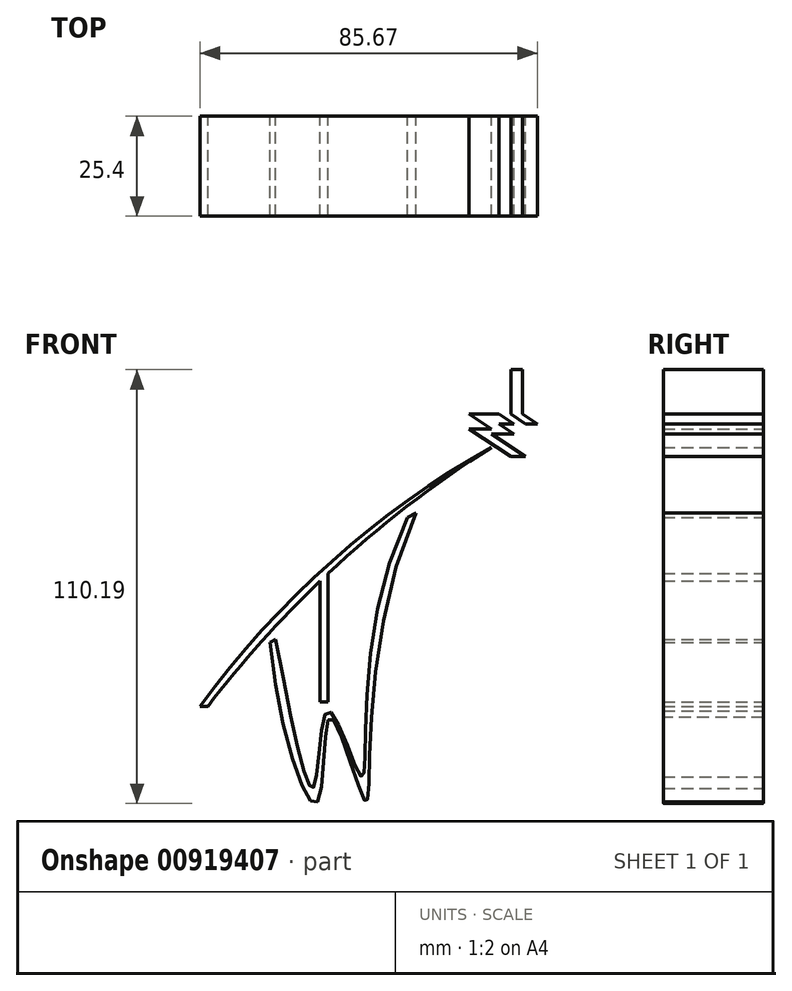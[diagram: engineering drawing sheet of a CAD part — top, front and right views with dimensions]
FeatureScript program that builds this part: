
annotation { "Feature Type Name" : "Feature", "Feature Type Description" : "" }
export const myFeature = defineFeature(function(context is Context, id is Id, definition is map)
    precondition{}
    {
        {
            var Q0;
            Q0=qCreatedBy(makeId("Front.planeOp"),FACE);
            var sketch = newSketch(context, id + "F0", { "sketchPlane" : qUnion([Q0])});
            skArc(sketch, "E0", {"start": v(27.94, 43.26) * mm, "mid": v(-11, 13.56) * mm, "end": v(-44.09, -22.54) * mm});
            skArc(sketch, "E1", {"start": v(27.94, 43.26) * mm, "mid": v(-12.59, 14.34) * mm, "end": v(-46.04, -22.54) * mm});
            skLineSegment(sketch, "E2", {"start": v(-46.04, -22.54) * mm, "end": v(-44.09, -22.54) * mm});
            skLineSegment(sketch, "E3", {"start": v(-15.57, 9.3) * mm, "end": v(-15.57, -21.37) * mm});
            skLineSegment(sketch, "E4", {"start": v(-15.57, -21.37) * mm, "end": v(-13.53, -21.37) * mm});
            skLineSegment(sketch, "E5", {"start": v(-13.53, -21.37) * mm, "end": v(-13.53, 11.23) * mm});
            skArc(sketch, "E6", {"start": v(27.94, 43.26) * mm, "mid": v(6.63, 28) * mm, "end": v(-13.53, 11.23) * mm});
            skArc(sketch, "E7", {"start": v(-15.57, 9.3) * mm, "mid": v(-30.23, -6.26) * mm, "end": v(-44.09, -22.54) * mm});
            skPoint(sketch, "E8.4.internal.snap0", {"position": v(-30.23, -6.26) * mm});
            skFitSpline(sketch, "E8", {"points": [v(8.74, 26.62) * mm, v(-4.43, -46.23) * mm, v(-12.97, -25.36) * mm, v(-16.13, -46.57) * mm, v(-28.33, -6.26) * mm], "startDerivative": vector(-136.03, -313.45) * mm, "endDerivative": vector(-22.87, 244.76) * mm});
            skPoint(sketch, "E9.0.internal.snap0", {"position": v(6.63, 28) * mm});
            skFitSpline(sketch, "E9", {"points": [v(6.63, 25.41) * mm, v(-5.36, -40.08) * mm, v(-13.53, -23.7) * mm, v(-17.03, -42.75) * mm, v(-26.85, -5.57) * mm], "startDerivative": vector(-126.44, -255.91) * mm, "endDerivative": vector(-44.36, 231) * mm});
            skLineSegment(sketch, "E10", {"start": v(-28.33, -6.26) * mm, "end": v(-26.85, -5.57) * mm});
            skLineSegment(sketch, "E11", {"start": v(6.63, 25.41) * mm, "end": v(8.74, 26.62) * mm});
            skArc(sketch, "E12", {"start": v(-19.48, 13.87) * mm, "mid": v(-23.54, 31.95) * mm, "end": v(-12.13, 17.35) * mm});
            skArc(sketch, "E13", {"start": v(-19.48, 11.53) * mm, "mid": v(-25.21, 33.72) * mm, "end": v(-9.43, 17.1) * mm});
            skLineSegment(sketch, "E14", {"start": v(-19.48, 13.87) * mm, "end": v(-19.48, 11.53) * mm});
            skLineSegment(sketch, "E15", {"start": v(-12.13, 17.35) * mm, "end": v(-9.43, 17.1) * mm});
            skLineSegment(sketch, "E16", {"start": v(32.91, 40.98) * mm, "end": v(22.26, 47.99) * mm});
            skLineSegment(sketch, "E17", {"start": v(22.26, 47.99) * mm, "end": v(27.94, 47.99) * mm});
            skLineSegment(sketch, "E18", {"start": v(27.94, 47.99) * mm, "end": v(22.26, 51.72) * mm});
            skLineSegment(sketch, "E19", {"start": v(22.26, 51.72) * mm, "end": v(29.9, 51.72) * mm});
            skLineSegment(sketch, "E20", {"start": v(29.9, 51.72) * mm, "end": v(33.7, 49.22) * mm});
            skLineSegment(sketch, "E21", {"start": v(33.7, 49.22) * mm, "end": v(29.9, 49.22) * mm});
            skLineSegment(sketch, "E22", {"start": v(29.9, 49.22) * mm, "end": v(33.7, 46.72) * mm});
            skLineSegment(sketch, "E23", {"start": v(33.7, 46.72) * mm, "end": v(27.94, 46.72) * mm});
            skLineSegment(sketch, "E24", {"start": v(27.94, 46.72) * mm, "end": v(36.66, 40.98) * mm});
            skLineSegment(sketch, "E25", {"start": v(36.66, 40.98) * mm, "end": v(32.91, 40.98) * mm});
            skLineSegment(sketch, "E26", {"start": v(32.91, 51.72) * mm, "end": v(36.66, 49.26) * mm});
            skLineSegment(sketch, "E27", {"start": v(36.66, 49.26) * mm, "end": v(39.63, 49.26) * mm});
            skLineSegment(sketch, "E28", {"start": v(39.63, 49.26) * mm, "end": v(35.88, 51.72) * mm});
            skLineSegment(sketch, "E29", {"start": v(35.88, 51.72) * mm, "end": v(35.88, 63.02) * mm});
            skLineSegment(sketch, "E30", {"start": v(32.91, 63.02) * mm, "end": v(35.88, 63.02) * mm});
            skLineSegment(sketch, "E31", {"start": v(32.91, 63.02) * mm, "end": v(32.91, 51.72) * mm});
            skArc(sketch, "E32", {"start": v(30.61, 53.94) * mm, "mid": v(34.56, 72.86) * mm, "end": v(37.87, 53.82) * mm});
            skArc(sketch, "E33", {"start": v(30.61, 55.73) * mm, "mid": v(34.57, 71.23) * mm, "end": v(37.87, 55.58) * mm});
            skLineSegment(sketch, "E34", {"start": v(30.61, 55.73) * mm, "end": v(30.61, 53.94) * mm});
            skLineSegment(sketch, "E35", {"start": v(37.87, 55.58) * mm, "end": v(37.87, 53.82) * mm});
            skSolve(sketch);
        }
        {
            var Q0;
            Q0=makeQuery(id+"F0.imprint","IMPRINT",FACE,{"disambiguationData":[TD([[makeQuery(id+"F0.imprint","IMPRINT",EDGE,{"derivedFrom":sQuery(id+"F0.wireOp",EDGE,"E12")}),1.0]])]});
            var Q1;
            {var subQ6=sQuery(id+"F0.wireOp",EDGE,"E2");Q1=makeQuery(id+"F0.imprint","IMPRINT",FACE,{"disambiguationData":[TD([[makeQuery(id+"F0.imprint","IMPRINT",EDGE,{"derivedFrom":subQ6}),1.0]])]});}
            var Q2;
            {var subQ0=sQuery(id+"F0.wireOp",EDGE,"E3");Q2=makeQuery(id+"F0.imprint","IMPRINT",FACE,{"disambiguationData":[TD([[makeQuery(id+"F0.imprint","IMPRINT",EDGE,{"derivedFrom":subQ0}),1.0]])]});}
            var Q3;
            Q3=makeQuery(id+"F0.imprint","IMPRINT",FACE,{"disambiguationData":[TD([[makeQuery(id+"F0.imprint","IMPRINT",EDGE,{"derivedFrom":sQuery(id+"F0.wireOp",EDGE,"E8")}),-1.0]])]});
            var Q4;
            Q4=makeQuery(id+"F0.imprint","IMPRINT",FACE,{"disambiguationData":[TD([[makeQuery(id+"F0.imprint","IMPRINT",EDGE,{"derivedFrom":sQuery(id+"F0.wireOp",EDGE,"E16")}),-1.0]])]});
            var Q5;
            Q5=makeQuery(id+"F0.imprint","IMPRINT",FACE,{"disambiguationData":[TD([[makeQuery(id+"F0.imprint","IMPRINT",EDGE,{"derivedFrom":sQuery(id+"F0.wireOp",EDGE,"E26")}),1.0]])]});
            var Q6;
            Q6=makeQuery(id+"F0.imprint","IMPRINT",FACE,{"disambiguationData":[TD([[makeQuery(id+"F0.imprint","IMPRINT",EDGE,{"derivedFrom":sQuery(id+"F0.wireOp",EDGE,"E32")}),-1.0]])]});
            extrude(context, id + "F1", {"entities" : qUnion([Q0, Q1, Q2, Q3, Q4, Q5, Q6]), "depth" : 25.4 * mm, "offsetDistance" : 25.4 * mm});
        }
    });
